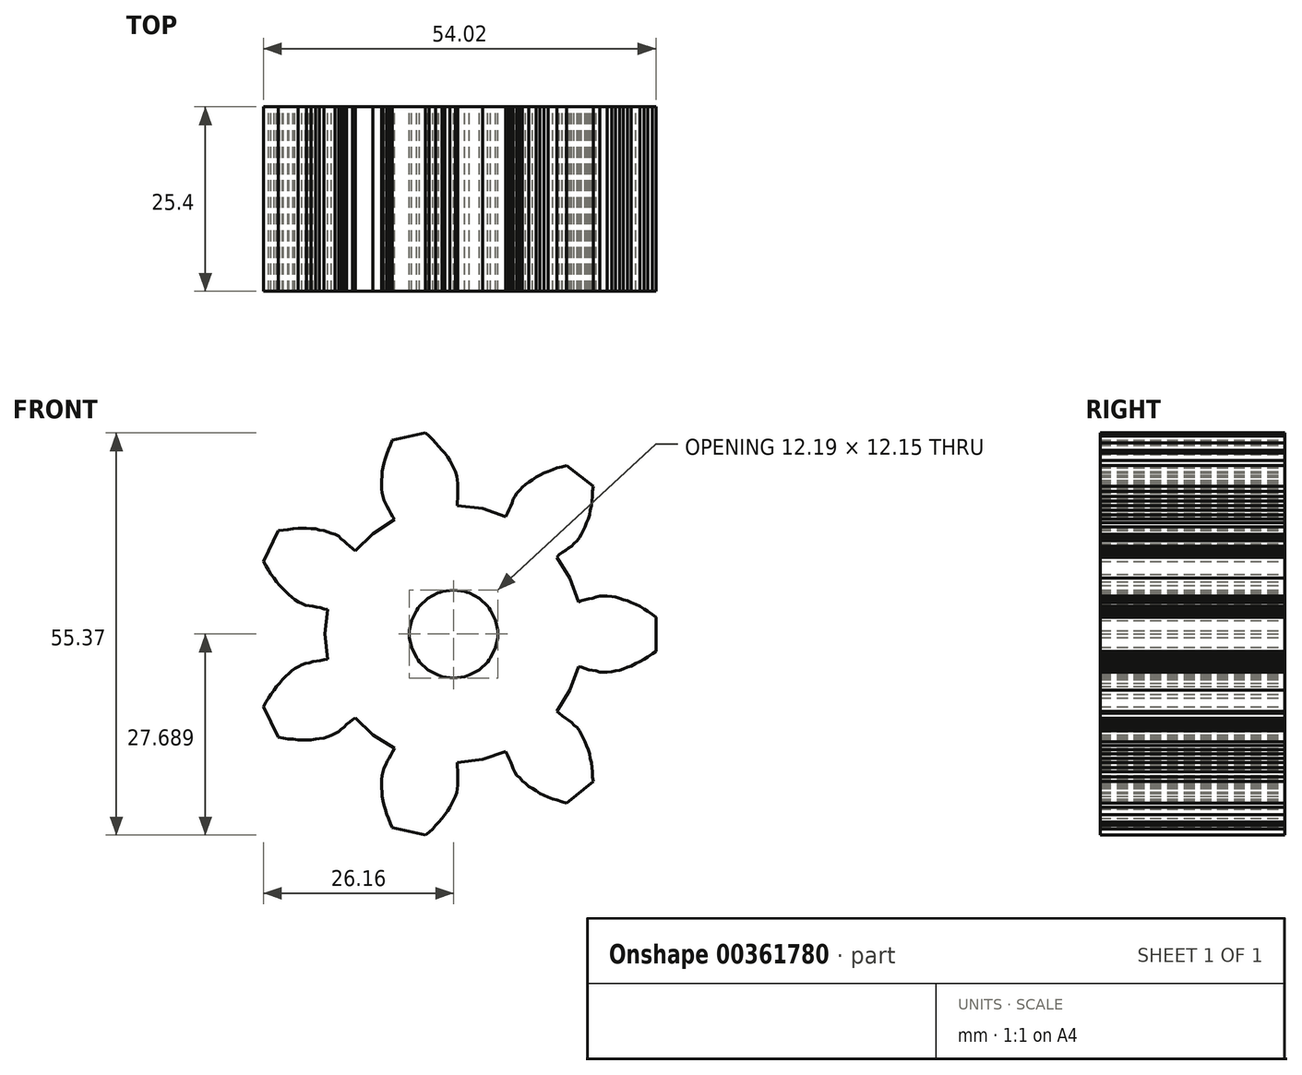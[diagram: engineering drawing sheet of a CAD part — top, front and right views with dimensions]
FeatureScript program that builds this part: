
annotation { "Feature Type Name" : "Feature", "Feature Type Description" : "" }
export const myFeature = defineFeature(function(context is Context, id is Id, definition is map)
    precondition{}
    {
        {
            var Q0;
            Q0=qCreatedBy(makeId("Front.planeOp"),FACE);
            var sketch = newSketch(context, id + "F0", { "sketchPlane" : qUnion([Q0])});
            skLineSegment(sketch, "E0", {"start": v(-98.04, 127.68) * mm, "end": v(-97.87, 127.68) * mm});
            skLineSegment(sketch, "E1", {"start": v(5.93, 25.9) * mm, "end": v(5.93, 25.45) * mm});
            skLineSegment(sketch, "E2", {"start": v(5.93, 25.45) * mm, "end": v(5.62, 24.07) * mm});
            skLineSegment(sketch, "E3", {"start": v(5.62, 24.07) * mm, "end": v(4.93, 22.63) * mm});
            skLineSegment(sketch, "E4", {"start": v(4.93, 22.63) * mm, "end": v(4.74, 22.35) * mm});
            skLineSegment(sketch, "E5", {"start": v(4.74, 22.35) * mm, "end": v(4.55, 22.08) * mm});
            skLineSegment(sketch, "E6", {"start": v(4.55, 22.08) * mm, "end": v(3.4, 21) * mm});
            skLineSegment(sketch, "E7", {"start": v(3.4, 21) * mm, "end": v(2, 20.26) * mm});
            skLineSegment(sketch, "E8", {"start": v(2, 20.26) * mm, "end": v(1.7, 20.15) * mm});
            skLineSegment(sketch, "E9", {"start": v(1.7, 20.15) * mm, "end": v(1.37, 20.05) * mm});
            skLineSegment(sketch, "E10", {"start": v(1.37, 20.05) * mm, "end": v(-0.17, 19.83) * mm});
            skLineSegment(sketch, "E11", {"start": v(-0.17, 19.83) * mm, "end": v(-1.72, 20.05) * mm});
            skLineSegment(sketch, "E12", {"start": v(-1.72, 20.05) * mm, "end": v(-2.03, 20.15) * mm});
            skLineSegment(sketch, "E13", {"start": v(-2.03, 20.15) * mm, "end": v(-2.35, 20.26) * mm});
            skLineSegment(sketch, "E14", {"start": v(-2.35, 20.26) * mm, "end": v(-3.75, 21) * mm});
            skLineSegment(sketch, "E15", {"start": v(-3.75, 21) * mm, "end": v(-4.9, 22.08) * mm});
            skLineSegment(sketch, "E16", {"start": v(-4.9, 22.08) * mm, "end": v(-5.08, 22.35) * mm});
            skLineSegment(sketch, "E17", {"start": v(-5.08, 22.35) * mm, "end": v(-5.27, 22.63) * mm});
            skLineSegment(sketch, "E18", {"start": v(-5.27, 22.63) * mm, "end": v(-5.96, 24.07) * mm});
            skLineSegment(sketch, "E19", {"start": v(-5.96, 24.07) * mm, "end": v(-6.27, 25.45) * mm});
            skLineSegment(sketch, "E20", {"start": v(-6.27, 25.45) * mm, "end": v(-6.27, 25.9) * mm});
            skLineSegment(sketch, "E21", {"start": v(-6.27, 25.9) * mm, "end": v(-6.27, 26.37) * mm});
            skLineSegment(sketch, "E22", {"start": v(-6.27, 26.37) * mm, "end": v(-5.96, 27.75) * mm});
            skLineSegment(sketch, "E23", {"start": v(-5.96, 27.75) * mm, "end": v(-5.27, 29.2) * mm});
            skLineSegment(sketch, "E24", {"start": v(-5.27, 29.2) * mm, "end": v(-5.08, 29.46) * mm});
            skLineSegment(sketch, "E25", {"start": v(-5.08, 29.46) * mm, "end": v(-4.9, 29.74) * mm});
            skLineSegment(sketch, "E26", {"start": v(-4.9, 29.74) * mm, "end": v(-3.75, 30.82) * mm});
            skLineSegment(sketch, "E27", {"start": v(-3.75, 30.82) * mm, "end": v(-2.35, 31.56) * mm});
            skLineSegment(sketch, "E28", {"start": v(-2.35, 31.56) * mm, "end": v(-2.03, 31.67) * mm});
            skLineSegment(sketch, "E29", {"start": v(-2.03, 31.67) * mm, "end": v(-1.72, 31.77) * mm});
            skLineSegment(sketch, "E30", {"start": v(-1.72, 31.77) * mm, "end": v(-0.17, 31.98) * mm});
            skLineSegment(sketch, "E31", {"start": v(-0.17, 31.98) * mm, "end": v(1.37, 31.77) * mm});
            skLineSegment(sketch, "E32", {"start": v(1.37, 31.77) * mm, "end": v(1.7, 31.67) * mm});
            skLineSegment(sketch, "E33", {"start": v(1.7, 31.67) * mm, "end": v(2, 31.56) * mm});
            skLineSegment(sketch, "E34", {"start": v(2, 31.56) * mm, "end": v(3.4, 30.82) * mm});
            skLineSegment(sketch, "E35", {"start": v(3.4, 30.82) * mm, "end": v(4.55, 29.74) * mm});
            skLineSegment(sketch, "E36", {"start": v(4.55, 29.74) * mm, "end": v(4.74, 29.46) * mm});
            skLineSegment(sketch, "E37", {"start": v(4.74, 29.46) * mm, "end": v(4.93, 29.2) * mm});
            skLineSegment(sketch, "E38", {"start": v(4.93, 29.2) * mm, "end": v(5.62, 27.75) * mm});
            skLineSegment(sketch, "E39", {"start": v(5.62, 27.75) * mm, "end": v(5.93, 26.37) * mm});
            skLineSegment(sketch, "E40", {"start": v(5.93, 26.37) * mm, "end": v(5.93, 25.9) * mm});
            skLineSegment(sketch, "E41", {"start": v(15.83, 18.2) * mm, "end": v(17.02, 21.42) * mm});
            skLineSegment(sketch, "E42", {"start": v(17.02, 21.42) * mm, "end": v(17.44, 21.34) * mm});
            skLineSegment(sketch, "E43", {"start": v(17.44, 21.34) * mm, "end": v(17.95, 21.17) * mm});
            skLineSegment(sketch, "E44", {"start": v(17.95, 21.17) * mm, "end": v(18.46, 21) * mm});
            skLineSegment(sketch, "E45", {"start": v(18.46, 21) * mm, "end": v(18.97, 20.91) * mm});
            skLineSegment(sketch, "E46", {"start": v(18.97, 20.91) * mm, "end": v(19.47, 20.83) * mm});
            skLineSegment(sketch, "E47", {"start": v(19.47, 20.83) * mm, "end": v(19.98, 20.66) * mm});
            skLineSegment(sketch, "E48", {"start": v(19.98, 20.66) * mm, "end": v(20.49, 20.66) * mm});
            skLineSegment(sketch, "E49", {"start": v(20.49, 20.66) * mm, "end": v(21, 20.66) * mm});
            skLineSegment(sketch, "E50", {"start": v(21, 20.66) * mm, "end": v(21.6, 20.74) * mm});
            skLineSegment(sketch, "E51", {"start": v(21.6, 20.74) * mm, "end": v(22.1, 20.83) * mm});
            skLineSegment(sketch, "E52", {"start": v(22.1, 20.83) * mm, "end": v(22.69, 20.91) * mm});
            skLineSegment(sketch, "E53", {"start": v(22.69, 20.91) * mm, "end": v(23.2, 21.08) * mm});
            skLineSegment(sketch, "E54", {"start": v(23.2, 21.08) * mm, "end": v(23.8, 21.34) * mm});
            skLineSegment(sketch, "E55", {"start": v(23.8, 21.34) * mm, "end": v(24.3, 21.5) * mm});
            skLineSegment(sketch, "E56", {"start": v(24.3, 21.5) * mm, "end": v(24.9, 21.84) * mm});
            skLineSegment(sketch, "E57", {"start": v(24.9, 21.84) * mm, "end": v(25.48, 22.1) * mm});
            skLineSegment(sketch, "E58", {"start": v(25.48, 22.1) * mm, "end": v(26.08, 22.44) * mm});
            skLineSegment(sketch, "E59", {"start": v(26.08, 22.44) * mm, "end": v(26.59, 22.78) * mm});
            skLineSegment(sketch, "E60", {"start": v(26.59, 22.78) * mm, "end": v(27.18, 23.2) * mm});
            skLineSegment(sketch, "E61", {"start": v(27.18, 23.2) * mm, "end": v(27.69, 23.54) * mm});
            skLineSegment(sketch, "E62", {"start": v(27.69, 23.54) * mm, "end": v(27.69, 28.2) * mm});
            skLineSegment(sketch, "E63", {"start": v(27.69, 28.2) * mm, "end": v(27.18, 28.62) * mm});
            skLineSegment(sketch, "E64", {"start": v(27.18, 28.62) * mm, "end": v(26.59, 29.04) * mm});
            skLineSegment(sketch, "E65", {"start": v(26.59, 29.04) * mm, "end": v(26.08, 29.38) * mm});
            skLineSegment(sketch, "E66", {"start": v(26.08, 29.38) * mm, "end": v(25.48, 29.72) * mm});
            skLineSegment(sketch, "E67", {"start": v(25.48, 29.72) * mm, "end": v(24.9, 29.97) * mm});
            skLineSegment(sketch, "E68", {"start": v(24.9, 29.97) * mm, "end": v(24.3, 30.23) * mm});
            skLineSegment(sketch, "E69", {"start": v(24.3, 30.23) * mm, "end": v(23.8, 30.48) * mm});
            skLineSegment(sketch, "E70", {"start": v(23.8, 30.48) * mm, "end": v(23.2, 30.65) * mm});
            skLineSegment(sketch, "E71", {"start": v(23.2, 30.65) * mm, "end": v(22.69, 30.82) * mm});
            skLineSegment(sketch, "E72", {"start": v(22.69, 30.82) * mm, "end": v(22.1, 30.99) * mm});
            skLineSegment(sketch, "E73", {"start": v(22.1, 30.99) * mm, "end": v(21.6, 31.07) * mm});
            skLineSegment(sketch, "E74", {"start": v(21.6, 31.07) * mm, "end": v(21, 31.16) * mm});
            skLineSegment(sketch, "E75", {"start": v(21, 31.16) * mm, "end": v(20.49, 31.16) * mm});
            skLineSegment(sketch, "E76", {"start": v(20.49, 31.16) * mm, "end": v(19.98, 31.16) * mm});
            skLineSegment(sketch, "E77", {"start": v(19.98, 31.16) * mm, "end": v(19.47, 30.99) * mm});
            skLineSegment(sketch, "E78", {"start": v(19.47, 30.99) * mm, "end": v(18.97, 30.82) * mm});
            skLineSegment(sketch, "E79", {"start": v(18.97, 30.82) * mm, "end": v(18.46, 30.73) * mm});
            skLineSegment(sketch, "E80", {"start": v(18.46, 30.73) * mm, "end": v(17.95, 30.65) * mm});
            skLineSegment(sketch, "E81", {"start": v(17.95, 30.65) * mm, "end": v(17.44, 30.48) * mm});
            skLineSegment(sketch, "E82", {"start": v(17.44, 30.48) * mm, "end": v(17.02, 30.31) * mm});
            skLineSegment(sketch, "E83", {"start": v(17.02, 30.31) * mm, "end": v(15.83, 33.61) * mm});
            skLineSegment(sketch, "E84", {"start": v(15.83, 33.61) * mm, "end": v(14.06, 36.5) * mm});
            skLineSegment(sketch, "E85", {"start": v(14.06, 36.5) * mm, "end": v(14.4, 36.83) * mm});
            skLineSegment(sketch, "E86", {"start": v(14.4, 36.83) * mm, "end": v(14.82, 37.17) * mm});
            skLineSegment(sketch, "E87", {"start": v(14.82, 37.17) * mm, "end": v(15.24, 37.42) * mm});
            skLineSegment(sketch, "E88", {"start": v(15.24, 37.42) * mm, "end": v(15.66, 37.76) * mm});
            skLineSegment(sketch, "E89", {"start": v(15.66, 37.76) * mm, "end": v(16.09, 38.02) * mm});
            skLineSegment(sketch, "E90", {"start": v(16.09, 38.02) * mm, "end": v(16.43, 38.35) * mm});
            skLineSegment(sketch, "E91", {"start": v(16.43, 38.35) * mm, "end": v(16.85, 38.78) * mm});
            skLineSegment(sketch, "E92", {"start": v(16.85, 38.78) * mm, "end": v(17.19, 39.2) * mm});
            skLineSegment(sketch, "E93", {"start": v(17.19, 39.2) * mm, "end": v(17.44, 39.62) * mm});
            skLineSegment(sketch, "E94", {"start": v(17.44, 39.62) * mm, "end": v(17.7, 40.13) * mm});
            skLineSegment(sketch, "E95", {"start": v(17.7, 40.13) * mm, "end": v(17.95, 40.64) * mm});
            skLineSegment(sketch, "E96", {"start": v(17.95, 40.64) * mm, "end": v(18.12, 41.23) * mm});
            skLineSegment(sketch, "E97", {"start": v(18.12, 41.23) * mm, "end": v(18.37, 41.74) * mm});
            skLineSegment(sketch, "E98", {"start": v(18.37, 41.74) * mm, "end": v(18.54, 42.33) * mm});
            skLineSegment(sketch, "E99", {"start": v(18.54, 42.33) * mm, "end": v(18.63, 42.93) * mm});
            skLineSegment(sketch, "E100", {"start": v(18.63, 42.93) * mm, "end": v(18.8, 43.6) * mm});
            skLineSegment(sketch, "E101", {"start": v(18.8, 43.6) * mm, "end": v(18.88, 44.2) * mm});
            skLineSegment(sketch, "E102", {"start": v(18.88, 44.2) * mm, "end": v(18.97, 44.87) * mm});
            skLineSegment(sketch, "E103", {"start": v(18.97, 44.87) * mm, "end": v(18.97, 45.55) * mm});
            skLineSegment(sketch, "E104", {"start": v(18.97, 45.55) * mm, "end": v(19.05, 46.23) * mm});
            skLineSegment(sketch, "E105", {"start": v(19.05, 46.23) * mm, "end": v(15.4, 49.1) * mm});
            skLineSegment(sketch, "E106", {"start": v(15.4, 49.1) * mm, "end": v(14.73, 48.94) * mm});
            skLineSegment(sketch, "E107", {"start": v(14.73, 48.94) * mm, "end": v(14.06, 48.77) * mm});
            skLineSegment(sketch, "E108", {"start": v(14.06, 48.77) * mm, "end": v(13.46, 48.51) * mm});
            skLineSegment(sketch, "E109", {"start": v(13.46, 48.51) * mm, "end": v(12.87, 48.26) * mm});
            skLineSegment(sketch, "E110", {"start": v(12.87, 48.26) * mm, "end": v(12.28, 48.1) * mm});
            skLineSegment(sketch, "E111", {"start": v(12.28, 48.1) * mm, "end": v(11.68, 47.75) * mm});
            skLineSegment(sketch, "E112", {"start": v(11.68, 47.75) * mm, "end": v(11.18, 47.5) * mm});
            skLineSegment(sketch, "E113", {"start": v(11.18, 47.5) * mm, "end": v(10.67, 47.16) * mm});
            skLineSegment(sketch, "E114", {"start": v(10.67, 47.16) * mm, "end": v(10.16, 46.82) * mm});
            skLineSegment(sketch, "E115", {"start": v(10.16, 46.82) * mm, "end": v(9.74, 46.48) * mm});
            skLineSegment(sketch, "E116", {"start": v(9.74, 46.48) * mm, "end": v(9.31, 46.14) * mm});
            skLineSegment(sketch, "E117", {"start": v(9.31, 46.14) * mm, "end": v(8.97, 45.72) * mm});
            skLineSegment(sketch, "E118", {"start": v(8.97, 45.72) * mm, "end": v(8.55, 45.3) * mm});
            skLineSegment(sketch, "E119", {"start": v(8.55, 45.3) * mm, "end": v(8.3, 44.87) * mm});
            skLineSegment(sketch, "E120", {"start": v(8.3, 44.87) * mm, "end": v(8.04, 44.45) * mm});
            skLineSegment(sketch, "E121", {"start": v(8.04, 44.45) * mm, "end": v(7.87, 43.94) * mm});
            skLineSegment(sketch, "E122", {"start": v(7.87, 43.94) * mm, "end": v(7.7, 43.52) * mm});
            skLineSegment(sketch, "E123", {"start": v(7.7, 43.52) * mm, "end": v(7.45, 43.01) * mm});
            skLineSegment(sketch, "E124", {"start": v(7.45, 43.01) * mm, "end": v(7.28, 42.59) * mm});
            skLineSegment(sketch, "E125", {"start": v(7.28, 42.59) * mm, "end": v(7.03, 42.08) * mm});
            skLineSegment(sketch, "E126", {"start": v(7.03, 42.08) * mm, "end": v(3.8, 43.18) * mm});
            skLineSegment(sketch, "E127", {"start": v(3.8, 43.18) * mm, "end": v(0.34, 43.6) * mm});
            skLineSegment(sketch, "E128", {"start": v(0.34, 43.6) * mm, "end": v(0.34, 44.11) * mm});
            skLineSegment(sketch, "E129", {"start": v(0.34, 44.11) * mm, "end": v(0.42, 44.62) * mm});
            skLineSegment(sketch, "E130", {"start": v(0.42, 44.62) * mm, "end": v(0.42, 45.13) * mm});
            skLineSegment(sketch, "E131", {"start": v(0.42, 45.13) * mm, "end": v(0.42, 45.64) * mm});
            skLineSegment(sketch, "E132", {"start": v(0.42, 45.64) * mm, "end": v(0.42, 46.14) * mm});
            skLineSegment(sketch, "E133", {"start": v(0.42, 46.14) * mm, "end": v(0.42, 46.65) * mm});
            skLineSegment(sketch, "E134", {"start": v(0.42, 46.65) * mm, "end": v(0.34, 47.16) * mm});
            skLineSegment(sketch, "E135", {"start": v(0.34, 47.16) * mm, "end": v(0.25, 47.67) * mm});
            skLineSegment(sketch, "E136", {"start": v(0.25, 47.67) * mm, "end": v(0.08, 48.26) * mm});
            skLineSegment(sketch, "E137", {"start": v(0.08, 48.26) * mm, "end": v(-0.17, 48.77) * mm});
            skLineSegment(sketch, "E138", {"start": v(-0.17, 48.77) * mm, "end": v(-0.42, 49.28) * mm});
            skLineSegment(sketch, "E139", {"start": v(-0.42, 49.28) * mm, "end": v(-0.68, 49.78) * mm});
            skLineSegment(sketch, "E140", {"start": v(-0.68, 49.78) * mm, "end": v(-1.02, 50.3) * mm});
            skLineSegment(sketch, "E141", {"start": v(-1.02, 50.3) * mm, "end": v(-1.36, 50.8) * mm});
            skLineSegment(sketch, "E142", {"start": v(-1.36, 50.8) * mm, "end": v(-1.78, 51.22) * mm});
            skLineSegment(sketch, "E143", {"start": v(-1.78, 51.22) * mm, "end": v(-2.2, 51.73) * mm});
            skLineSegment(sketch, "E144", {"start": v(-2.2, 51.73) * mm, "end": v(-2.62, 52.24) * mm});
            skLineSegment(sketch, "E145", {"start": v(-2.62, 52.24) * mm, "end": v(-3.05, 52.66) * mm});
            skLineSegment(sketch, "E146", {"start": v(-3.05, 52.66) * mm, "end": v(-3.56, 53.17) * mm});
            skLineSegment(sketch, "E147", {"start": v(-3.56, 53.17) * mm, "end": v(-4.06, 53.6) * mm});
            skLineSegment(sketch, "E148", {"start": v(-4.06, 53.6) * mm, "end": v(-8.64, 52.58) * mm});
            skLineSegment(sketch, "E149", {"start": v(-8.64, 52.58) * mm, "end": v(-8.9, 51.9) * mm});
            skLineSegment(sketch, "E150", {"start": v(-8.9, 51.9) * mm, "end": v(-9.14, 51.3) * mm});
            skLineSegment(sketch, "E151", {"start": v(-9.14, 51.3) * mm, "end": v(-9.4, 50.63) * mm});
            skLineSegment(sketch, "E152", {"start": v(-9.4, 50.63) * mm, "end": v(-9.57, 50.04) * mm});
            skLineSegment(sketch, "E153", {"start": v(-9.57, 50.04) * mm, "end": v(-9.74, 49.44) * mm});
            skLineSegment(sketch, "E154", {"start": v(-9.74, 49.44) * mm, "end": v(-9.9, 48.85) * mm});
            skLineSegment(sketch, "E155", {"start": v(-9.9, 48.85) * mm, "end": v(-10, 48.26) * mm});
            skLineSegment(sketch, "E156", {"start": v(-10, 48.26) * mm, "end": v(-10, 47.67) * mm});
            skLineSegment(sketch, "E157", {"start": v(-10, 47.67) * mm, "end": v(-10.08, 47.07) * mm});
            skLineSegment(sketch, "E158", {"start": v(-10.08, 47.07) * mm, "end": v(-10.08, 46.48) * mm});
            skLineSegment(sketch, "E159", {"start": v(-10.08, 46.48) * mm, "end": v(-10.08, 45.89) * mm});
            skLineSegment(sketch, "E160", {"start": v(-10.08, 45.89) * mm, "end": v(-10, 45.38) * mm});
            skLineSegment(sketch, "E161", {"start": v(-10, 45.38) * mm, "end": v(-9.9, 44.87) * mm});
            skLineSegment(sketch, "E162", {"start": v(-9.9, 44.87) * mm, "end": v(-9.74, 44.37) * mm});
            skLineSegment(sketch, "E163", {"start": v(-9.74, 44.37) * mm, "end": v(-9.48, 43.86) * mm});
            skLineSegment(sketch, "E164", {"start": v(-9.48, 43.86) * mm, "end": v(-9.31, 43.43) * mm});
            skLineSegment(sketch, "E165", {"start": v(-9.31, 43.43) * mm, "end": v(-9.06, 43.01) * mm});
            skLineSegment(sketch, "E166", {"start": v(-9.06, 43.01) * mm, "end": v(-8.8, 42.5) * mm});
            skLineSegment(sketch, "E167", {"start": v(-8.8, 42.5) * mm, "end": v(-8.55, 42.08) * mm});
            skLineSegment(sketch, "E168", {"start": v(-8.55, 42.08) * mm, "end": v(-8.3, 41.66) * mm});
            skLineSegment(sketch, "E169", {"start": v(-8.3, 41.66) * mm, "end": v(-11.26, 39.7) * mm});
            skLineSegment(sketch, "E170", {"start": v(-11.26, 39.7) * mm, "end": v(-13.72, 37.34) * mm});
            skLineSegment(sketch, "E171", {"start": v(-13.72, 37.34) * mm, "end": v(-14.06, 37.68) * mm});
            skLineSegment(sketch, "E172", {"start": v(-14.06, 37.68) * mm, "end": v(-14.48, 38.02) * mm});
            skLineSegment(sketch, "E173", {"start": v(-14.48, 38.02) * mm, "end": v(-14.9, 38.35) * mm});
            skLineSegment(sketch, "E174", {"start": v(-14.9, 38.35) * mm, "end": v(-15.24, 38.7) * mm});
            skLineSegment(sketch, "E175", {"start": v(-15.24, 38.7) * mm, "end": v(-15.66, 39.03) * mm});
            skLineSegment(sketch, "E176", {"start": v(-15.66, 39.03) * mm, "end": v(-16, 39.37) * mm});
            skLineSegment(sketch, "E177", {"start": v(-16, 39.37) * mm, "end": v(-16.5, 39.62) * mm});
            skLineSegment(sketch, "E178", {"start": v(-16.5, 39.62) * mm, "end": v(-17.02, 39.8) * mm});
            skLineSegment(sketch, "E179", {"start": v(-17.02, 39.8) * mm, "end": v(-17.53, 39.96) * mm});
            skLineSegment(sketch, "E180", {"start": v(-17.53, 39.96) * mm, "end": v(-18.03, 40.13) * mm});
            skLineSegment(sketch, "E181", {"start": v(-18.03, 40.13) * mm, "end": v(-18.63, 40.22) * mm});
            skLineSegment(sketch, "E182", {"start": v(-18.63, 40.22) * mm, "end": v(-19.13, 40.39) * mm});
            skLineSegment(sketch, "E183", {"start": v(-19.13, 40.39) * mm, "end": v(-19.81, 40.39) * mm});
            skLineSegment(sketch, "E184", {"start": v(-19.81, 40.39) * mm, "end": v(-20.4, 40.47) * mm});
            skLineSegment(sketch, "E185", {"start": v(-20.4, 40.47) * mm, "end": v(-21, 40.47) * mm});
            skLineSegment(sketch, "E186", {"start": v(-21, 40.47) * mm, "end": v(-21.6, 40.47) * mm});
            skLineSegment(sketch, "E187", {"start": v(-21.6, 40.47) * mm, "end": v(-22.27, 40.39) * mm});
            skLineSegment(sketch, "E188", {"start": v(-22.27, 40.39) * mm, "end": v(-22.95, 40.3) * mm});
            skLineSegment(sketch, "E189", {"start": v(-22.95, 40.3) * mm, "end": v(-23.62, 40.22) * mm});
            skLineSegment(sketch, "E190", {"start": v(-23.62, 40.22) * mm, "end": v(-24.3, 40.13) * mm});
            skLineSegment(sketch, "E191", {"start": v(-24.3, 40.13) * mm, "end": v(-26.33, 35.9) * mm});
            skLineSegment(sketch, "E192", {"start": v(-26.33, 35.9) * mm, "end": v(-26, 35.3) * mm});
            skLineSegment(sketch, "E193", {"start": v(-26, 35.3) * mm, "end": v(-25.65, 34.71) * mm});
            skLineSegment(sketch, "E194", {"start": v(-25.65, 34.71) * mm, "end": v(-25.32, 34.12) * mm});
            skLineSegment(sketch, "E195", {"start": v(-25.32, 34.12) * mm, "end": v(-24.9, 33.61) * mm});
            skLineSegment(sketch, "E196", {"start": v(-24.9, 33.61) * mm, "end": v(-24.55, 33.1) * mm});
            skLineSegment(sketch, "E197", {"start": v(-24.55, 33.1) * mm, "end": v(-24.13, 32.6) * mm});
            skLineSegment(sketch, "E198", {"start": v(-24.13, 32.6) * mm, "end": v(-23.7, 32.17) * mm});
            skLineSegment(sketch, "E199", {"start": v(-23.7, 32.17) * mm, "end": v(-23.28, 31.75) * mm});
            skLineSegment(sketch, "E200", {"start": v(-23.28, 31.75) * mm, "end": v(-22.86, 31.33) * mm});
            skLineSegment(sketch, "E201", {"start": v(-22.86, 31.33) * mm, "end": v(-22.44, 30.99) * mm});
            skLineSegment(sketch, "E202", {"start": v(-22.44, 30.99) * mm, "end": v(-22.01, 30.65) * mm});
            skLineSegment(sketch, "E203", {"start": v(-22.01, 30.65) * mm, "end": v(-21.5, 30.31) * mm});
            skLineSegment(sketch, "E204", {"start": v(-21.5, 30.31) * mm, "end": v(-21.08, 30.14) * mm});
            skLineSegment(sketch, "E205", {"start": v(-21.08, 30.14) * mm, "end": v(-20.57, 29.89) * mm});
            skLineSegment(sketch, "E206", {"start": v(-20.57, 29.89) * mm, "end": v(-20.07, 29.8) * mm});
            skLineSegment(sketch, "E207", {"start": v(-20.07, 29.8) * mm, "end": v(-19.56, 29.72) * mm});
            skLineSegment(sketch, "E208", {"start": v(-19.56, 29.72) * mm, "end": v(-19.05, 29.63) * mm});
            skLineSegment(sketch, "E209", {"start": v(-19.05, 29.63) * mm, "end": v(-18.54, 29.55) * mm});
            skLineSegment(sketch, "E210", {"start": v(-18.54, 29.55) * mm, "end": v(-18.03, 29.38) * mm});
            skLineSegment(sketch, "E211", {"start": v(-18.03, 29.38) * mm, "end": v(-17.53, 29.3) * mm});
            skLineSegment(sketch, "E212", {"start": v(-17.53, 29.3) * mm, "end": v(-17.86, 25.9) * mm});
            skLineSegment(sketch, "E213", {"start": v(-17.86, 25.9) * mm, "end": v(-17.53, 22.44) * mm});
            skLineSegment(sketch, "E214", {"start": v(-17.53, 22.44) * mm, "end": v(-18.03, 22.35) * mm});
            skLineSegment(sketch, "E215", {"start": v(-18.03, 22.35) * mm, "end": v(-18.54, 22.27) * mm});
            skLineSegment(sketch, "E216", {"start": v(-18.54, 22.27) * mm, "end": v(-19.05, 22.18) * mm});
            skLineSegment(sketch, "E217", {"start": v(-19.05, 22.18) * mm, "end": v(-19.56, 22.1) * mm});
            skLineSegment(sketch, "E218", {"start": v(-19.56, 22.1) * mm, "end": v(-20.07, 21.93) * mm});
            skLineSegment(sketch, "E219", {"start": v(-20.07, 21.93) * mm, "end": v(-20.57, 21.84) * mm});
            skLineSegment(sketch, "E220", {"start": v(-20.57, 21.84) * mm, "end": v(-21.08, 21.67) * mm});
            skLineSegment(sketch, "E221", {"start": v(-21.08, 21.67) * mm, "end": v(-21.5, 21.42) * mm});
            skLineSegment(sketch, "E222", {"start": v(-21.5, 21.42) * mm, "end": v(-22.01, 21.17) * mm});
            skLineSegment(sketch, "E223", {"start": v(-22.01, 21.17) * mm, "end": v(-22.44, 20.83) * mm});
            skLineSegment(sketch, "E224", {"start": v(-22.44, 20.83) * mm, "end": v(-22.86, 20.49) * mm});
            skLineSegment(sketch, "E225", {"start": v(-22.86, 20.49) * mm, "end": v(-23.28, 20.07) * mm});
            skLineSegment(sketch, "E226", {"start": v(-23.28, 20.07) * mm, "end": v(-23.7, 19.64) * mm});
            skLineSegment(sketch, "E227", {"start": v(-23.7, 19.64) * mm, "end": v(-24.13, 19.13) * mm});
            skLineSegment(sketch, "E228", {"start": v(-24.13, 19.13) * mm, "end": v(-24.55, 18.71) * mm});
            skLineSegment(sketch, "E229", {"start": v(-24.55, 18.71) * mm, "end": v(-24.9, 18.2) * mm});
            skLineSegment(sketch, "E230", {"start": v(-24.9, 18.2) * mm, "end": v(-25.32, 17.61) * mm});
            skLineSegment(sketch, "E231", {"start": v(-25.32, 17.61) * mm, "end": v(-25.65, 17.1) * mm});
            skLineSegment(sketch, "E232", {"start": v(-25.65, 17.1) * mm, "end": v(-26, 16.5) * mm});
            skLineSegment(sketch, "E233", {"start": v(-26, 16.5) * mm, "end": v(-26.33, 15.92) * mm});
            skLineSegment(sketch, "E234", {"start": v(-26.33, 15.92) * mm, "end": v(-24.3, 11.68) * mm});
            skLineSegment(sketch, "E235", {"start": v(-24.3, 11.68) * mm, "end": v(-23.62, 11.6) * mm});
            skLineSegment(sketch, "E236", {"start": v(-23.62, 11.6) * mm, "end": v(-22.95, 11.43) * mm});
            skLineSegment(sketch, "E237", {"start": v(-22.95, 11.43) * mm, "end": v(-22.27, 11.43) * mm});
            skLineSegment(sketch, "E238", {"start": v(-22.27, 11.43) * mm, "end": v(-21.6, 11.34) * mm});
            skLineSegment(sketch, "E239", {"start": v(-21.6, 11.34) * mm, "end": v(-21, 11.34) * mm});
            skLineSegment(sketch, "E240", {"start": v(-21, 11.34) * mm, "end": v(-20.4, 11.34) * mm});
            skLineSegment(sketch, "E241", {"start": v(-20.4, 11.34) * mm, "end": v(-19.81, 11.34) * mm});
            skLineSegment(sketch, "E242", {"start": v(-19.81, 11.34) * mm, "end": v(-19.13, 11.43) * mm});
            skLineSegment(sketch, "E243", {"start": v(-19.13, 11.43) * mm, "end": v(-18.63, 11.51) * mm});
            skLineSegment(sketch, "E244", {"start": v(-18.63, 11.51) * mm, "end": v(-18.03, 11.6) * mm});
            skLineSegment(sketch, "E245", {"start": v(-18.03, 11.6) * mm, "end": v(-17.53, 11.77) * mm});
            skLineSegment(sketch, "E246", {"start": v(-17.53, 11.77) * mm, "end": v(-17.02, 11.94) * mm});
            skLineSegment(sketch, "E247", {"start": v(-17.02, 11.94) * mm, "end": v(-16.5, 12.2) * mm});
            skLineSegment(sketch, "E248", {"start": v(-16.5, 12.2) * mm, "end": v(-16, 12.45) * mm});
            skLineSegment(sketch, "E249", {"start": v(-16, 12.45) * mm, "end": v(-15.66, 12.78) * mm});
            skLineSegment(sketch, "E250", {"start": v(-15.66, 12.78) * mm, "end": v(-15.24, 13.12) * mm});
            skLineSegment(sketch, "E251", {"start": v(-15.24, 13.12) * mm, "end": v(-14.9, 13.46) * mm});
            skLineSegment(sketch, "E252", {"start": v(-14.9, 13.46) * mm, "end": v(-14.48, 13.8) * mm});
            skLineSegment(sketch, "E253", {"start": v(-14.48, 13.8) * mm, "end": v(-14.06, 14.14) * mm});
            skLineSegment(sketch, "E254", {"start": v(-14.06, 14.14) * mm, "end": v(-13.72, 14.4) * mm});
            skLineSegment(sketch, "E255", {"start": v(-13.72, 14.4) * mm, "end": v(-11.26, 12.02) * mm});
            skLineSegment(sketch, "E256", {"start": v(-11.26, 12.02) * mm, "end": v(-8.3, 10.16) * mm});
            skLineSegment(sketch, "E257", {"start": v(-8.3, 10.16) * mm, "end": v(-8.55, 9.74) * mm});
            skLineSegment(sketch, "E258", {"start": v(-8.55, 9.74) * mm, "end": v(-8.8, 9.23) * mm});
            skLineSegment(sketch, "E259", {"start": v(-8.8, 9.23) * mm, "end": v(-9.06, 8.8) * mm});
            skLineSegment(sketch, "E260", {"start": v(-9.06, 8.8) * mm, "end": v(-9.31, 8.38) * mm});
            skLineSegment(sketch, "E261", {"start": v(-9.31, 8.38) * mm, "end": v(-9.48, 7.87) * mm});
            skLineSegment(sketch, "E262", {"start": v(-9.48, 7.87) * mm, "end": v(-9.74, 7.45) * mm});
            skLineSegment(sketch, "E263", {"start": v(-9.74, 7.45) * mm, "end": v(-9.9, 6.94) * mm});
            skLineSegment(sketch, "E264", {"start": v(-9.9, 6.94) * mm, "end": v(-10, 6.43) * mm});
            skLineSegment(sketch, "E265", {"start": v(-10, 6.43) * mm, "end": v(-10.08, 5.84) * mm});
            skLineSegment(sketch, "E266", {"start": v(-10.08, 5.84) * mm, "end": v(-10.08, 5.33) * mm});
            skLineSegment(sketch, "E267", {"start": v(-10.08, 5.33) * mm, "end": v(-10.08, 4.74) * mm});
            skLineSegment(sketch, "E268", {"start": v(-10.08, 4.74) * mm, "end": v(-10, 4.15) * mm});
            skLineSegment(sketch, "E269", {"start": v(-10, 4.15) * mm, "end": v(-10, 3.56) * mm});
            skLineSegment(sketch, "E270", {"start": v(-10, 3.56) * mm, "end": v(-9.9, 2.96) * mm});
            skLineSegment(sketch, "E271", {"start": v(-9.9, 2.96) * mm, "end": v(-9.74, 2.37) * mm});
            skLineSegment(sketch, "E272", {"start": v(-9.74, 2.37) * mm, "end": v(-9.57, 1.78) * mm});
            skLineSegment(sketch, "E273", {"start": v(-9.57, 1.78) * mm, "end": v(-9.4, 1.1) * mm});
            skLineSegment(sketch, "E274", {"start": v(-9.4, 1.1) * mm, "end": v(-9.14, 0.5) * mm});
            skLineSegment(sketch, "E275", {"start": v(-9.14, 0.5) * mm, "end": v(-8.9, -0.17) * mm});
            skLineSegment(sketch, "E276", {"start": v(-8.9, -0.17) * mm, "end": v(-8.64, -0.76) * mm});
            skLineSegment(sketch, "E277", {"start": v(-8.64, -0.76) * mm, "end": v(-4.06, -1.78) * mm});
            skLineSegment(sketch, "E278", {"start": v(-4.06, -1.78) * mm, "end": v(-3.56, -1.36) * mm});
            skLineSegment(sketch, "E279", {"start": v(-3.56, -1.36) * mm, "end": v(-3.05, -0.93) * mm});
            skLineSegment(sketch, "E280", {"start": v(-3.05, -0.93) * mm, "end": v(-2.62, -0.42) * mm});
            skLineSegment(sketch, "E281", {"start": v(-2.62, -0.42) * mm, "end": v(-2.2, 0) * mm});
            skLineSegment(sketch, "E282", {"start": v(-2.2, 0) * mm, "end": v(-1.78, 0.5) * mm});
            skLineSegment(sketch, "E283", {"start": v(-1.78, 0.5) * mm, "end": v(-1.36, 1.02) * mm});
            skLineSegment(sketch, "E284", {"start": v(-1.36, 1.02) * mm, "end": v(-1.02, 1.52) * mm});
            skLineSegment(sketch, "E285", {"start": v(-1.02, 1.52) * mm, "end": v(-0.68, 2.03) * mm});
            skLineSegment(sketch, "E286", {"start": v(-0.68, 2.03) * mm, "end": v(-0.42, 2.54) * mm});
            skLineSegment(sketch, "E287", {"start": v(-0.42, 2.54) * mm, "end": v(-0.17, 3.05) * mm});
            skLineSegment(sketch, "E288", {"start": v(-0.17, 3.05) * mm, "end": v(0.08, 3.56) * mm});
            skLineSegment(sketch, "E289", {"start": v(0.08, 3.56) * mm, "end": v(0.25, 4.06) * mm});
            skLineSegment(sketch, "E290", {"start": v(0.25, 4.06) * mm, "end": v(0.34, 4.57) * mm});
            skLineSegment(sketch, "E291", {"start": v(0.34, 4.57) * mm, "end": v(0.42, 5.08) * mm});
            skLineSegment(sketch, "E292", {"start": v(0.42, 5.08) * mm, "end": v(0.42, 5.59) * mm});
            skLineSegment(sketch, "E293", {"start": v(0.42, 5.59) * mm, "end": v(0.42, 6.1) * mm});
            skLineSegment(sketch, "E294", {"start": v(0.42, 6.1) * mm, "end": v(0.42, 6.6) * mm});
            skLineSegment(sketch, "E295", {"start": v(0.42, 6.6) * mm, "end": v(0.42, 7.11) * mm});
            skLineSegment(sketch, "E296", {"start": v(0.42, 7.11) * mm, "end": v(0.34, 7.62) * mm});
            skLineSegment(sketch, "E297", {"start": v(0.34, 7.62) * mm, "end": v(0.34, 8.21) * mm});
            skLineSegment(sketch, "E298", {"start": v(0.34, 8.21) * mm, "end": v(3.8, 8.64) * mm});
            skLineSegment(sketch, "E299", {"start": v(3.8, 8.64) * mm, "end": v(7.03, 9.74) * mm});
            skLineSegment(sketch, "E300", {"start": v(7.03, 9.74) * mm, "end": v(7.28, 9.23) * mm});
            skLineSegment(sketch, "E301", {"start": v(7.28, 9.23) * mm, "end": v(7.45, 8.8) * mm});
            skLineSegment(sketch, "E302", {"start": v(7.45, 8.8) * mm, "end": v(7.7, 8.3) * mm});
            skLineSegment(sketch, "E303", {"start": v(7.7, 8.3) * mm, "end": v(7.87, 7.79) * mm});
            skLineSegment(sketch, "E304", {"start": v(7.87, 7.79) * mm, "end": v(8.04, 7.37) * mm});
            skLineSegment(sketch, "E305", {"start": v(8.04, 7.37) * mm, "end": v(8.3, 6.86) * mm});
            skLineSegment(sketch, "E306", {"start": v(8.3, 6.86) * mm, "end": v(8.55, 6.43) * mm});
            skLineSegment(sketch, "E307", {"start": v(8.55, 6.43) * mm, "end": v(8.97, 6.1) * mm});
            skLineSegment(sketch, "E308", {"start": v(8.97, 6.1) * mm, "end": v(9.31, 5.67) * mm});
            skLineSegment(sketch, "E309", {"start": v(9.31, 5.67) * mm, "end": v(9.74, 5.33) * mm});
            skLineSegment(sketch, "E310", {"start": v(9.74, 5.33) * mm, "end": v(10.16, 4.91) * mm});
            skLineSegment(sketch, "E311", {"start": v(10.16, 4.91) * mm, "end": v(10.67, 4.66) * mm});
            skLineSegment(sketch, "E312", {"start": v(10.67, 4.66) * mm, "end": v(11.18, 4.32) * mm});
            skLineSegment(sketch, "E313", {"start": v(11.18, 4.32) * mm, "end": v(11.68, 3.98) * mm});
            skLineSegment(sketch, "E314", {"start": v(11.68, 3.98) * mm, "end": v(12.28, 3.73) * mm});
            skLineSegment(sketch, "E315", {"start": v(12.28, 3.73) * mm, "end": v(12.87, 3.47) * mm});
            skLineSegment(sketch, "E316", {"start": v(12.87, 3.47) * mm, "end": v(13.46, 3.22) * mm});
            skLineSegment(sketch, "E317", {"start": v(13.46, 3.22) * mm, "end": v(14.06, 3.05) * mm});
            skLineSegment(sketch, "E318", {"start": v(14.06, 3.05) * mm, "end": v(14.73, 2.8) * mm});
            skLineSegment(sketch, "E319", {"start": v(14.73, 2.8) * mm, "end": v(15.4, 2.62) * mm});
            skLineSegment(sketch, "E320", {"start": v(15.4, 2.62) * mm, "end": v(19.05, 5.59) * mm});
            skLineSegment(sketch, "E321", {"start": v(19.05, 5.59) * mm, "end": v(18.97, 6.27) * mm});
            skLineSegment(sketch, "E322", {"start": v(18.97, 6.27) * mm, "end": v(18.97, 6.94) * mm});
            skLineSegment(sketch, "E323", {"start": v(18.97, 6.94) * mm, "end": v(18.88, 7.54) * mm});
            skLineSegment(sketch, "E324", {"start": v(18.88, 7.54) * mm, "end": v(18.8, 8.21) * mm});
            skLineSegment(sketch, "E325", {"start": v(18.8, 8.21) * mm, "end": v(18.63, 8.8) * mm});
            skLineSegment(sketch, "E326", {"start": v(18.63, 8.8) * mm, "end": v(18.54, 9.4) * mm});
            skLineSegment(sketch, "E327", {"start": v(18.54, 9.4) * mm, "end": v(18.37, 10) * mm});
            skLineSegment(sketch, "E328", {"start": v(18.37, 10) * mm, "end": v(18.12, 10.58) * mm});
            skLineSegment(sketch, "E329", {"start": v(18.12, 10.58) * mm, "end": v(17.95, 11.1) * mm});
            skLineSegment(sketch, "E330", {"start": v(17.95, 11.1) * mm, "end": v(17.7, 11.6) * mm});
            skLineSegment(sketch, "E331", {"start": v(17.7, 11.6) * mm, "end": v(17.44, 12.1) * mm});
            skLineSegment(sketch, "E332", {"start": v(17.44, 12.1) * mm, "end": v(17.19, 12.62) * mm});
            skLineSegment(sketch, "E333", {"start": v(17.19, 12.62) * mm, "end": v(16.85, 13.04) * mm});
            skLineSegment(sketch, "E334", {"start": v(16.85, 13.04) * mm, "end": v(16.43, 13.38) * mm});
            skLineSegment(sketch, "E335", {"start": v(16.43, 13.38) * mm, "end": v(16.09, 13.72) * mm});
            skLineSegment(sketch, "E336", {"start": v(16.09, 13.72) * mm, "end": v(15.66, 14.06) * mm});
            skLineSegment(sketch, "E337", {"start": v(15.66, 14.06) * mm, "end": v(15.24, 14.3) * mm});
            skLineSegment(sketch, "E338", {"start": v(15.24, 14.3) * mm, "end": v(14.82, 14.65) * mm});
            skLineSegment(sketch, "E339", {"start": v(14.82, 14.65) * mm, "end": v(14.4, 14.99) * mm});
            skLineSegment(sketch, "E340", {"start": v(14.4, 14.99) * mm, "end": v(14.06, 15.24) * mm});
            skLineSegment(sketch, "E341", {"start": v(14.06, 15.24) * mm, "end": v(15.83, 18.2) * mm});
            skSolve(sketch);
        }
        {
            var Q0;
            Q0=makeQuery(id+"F0.imprint","IMPRINT",FACE,{"disambiguationData":[TD([[makeQuery(id+"F0.imprint","IMPRINT",EDGE,{"derivedFrom":sQuery(id+"F0.wireOp",EDGE,"E1")}),1.0]])]});
            extrude(context, id + "F1", {"entities" : qUnion([Q0]), "depth" : 25.4 * mm});
        }
    });
